# Revit family: Sten Rund Liten
name_source: partatom
category: Furniture
units: mm (PartAtom-declared; Revit-internal decimal feet)

## family parameters
Always vertical = Yes
Cut with Voids When Loaded = No
OmniClass Number = 23.40.20.00
OmniClass Title = General Furniture and Specialties
Room Calculation Point = No
Shared = No
Work Plane-Based = No

## types (1)
- Sten Rund Liten
    CSI MasterFormat 2014 Code = 12 00 00
    CSI MasterFormat 2014 Title = Furnishings
    Default Elevation = 0 mm  [stored 0 ft]
    Depth = 560 mm
    Description = Sten sitting pouf
    Edition number = 1
    Height = 440 mm
    IFC Classification = Furniture
    Keynote = Sten, Furniture, Möbler, Sono
    Length = 560 mm
    Manufacturer = Tranås Skolmöbler
    ManufacturerName = Tranås Skolmöbler
    ManufacturerURL = https://www.tranasskolmobler.se
    Model = Sten Rund Liten
    OmniClass Code = 23-40 20 00
    OmniClass Description = General Furniture
    Primary Material = Frabric gray
    Product SKU = L10464
    Product group = Sten System
    Product name = Sten Rund Liten
    Secondary Material = Birch white
    URL = https://katalog.sonobrands.se
    Uniclass 2015 Code = EF_40_30
    Uniclass 2015 Name = Furnishings

note: [stored X ft] marks values corroborated as IEEE doubles in the binary element streams (Revit-internal decimal feet)

## geometry (parser evidence)
native form markers: Sweep x3
no freeform markers — native parametric forms only
